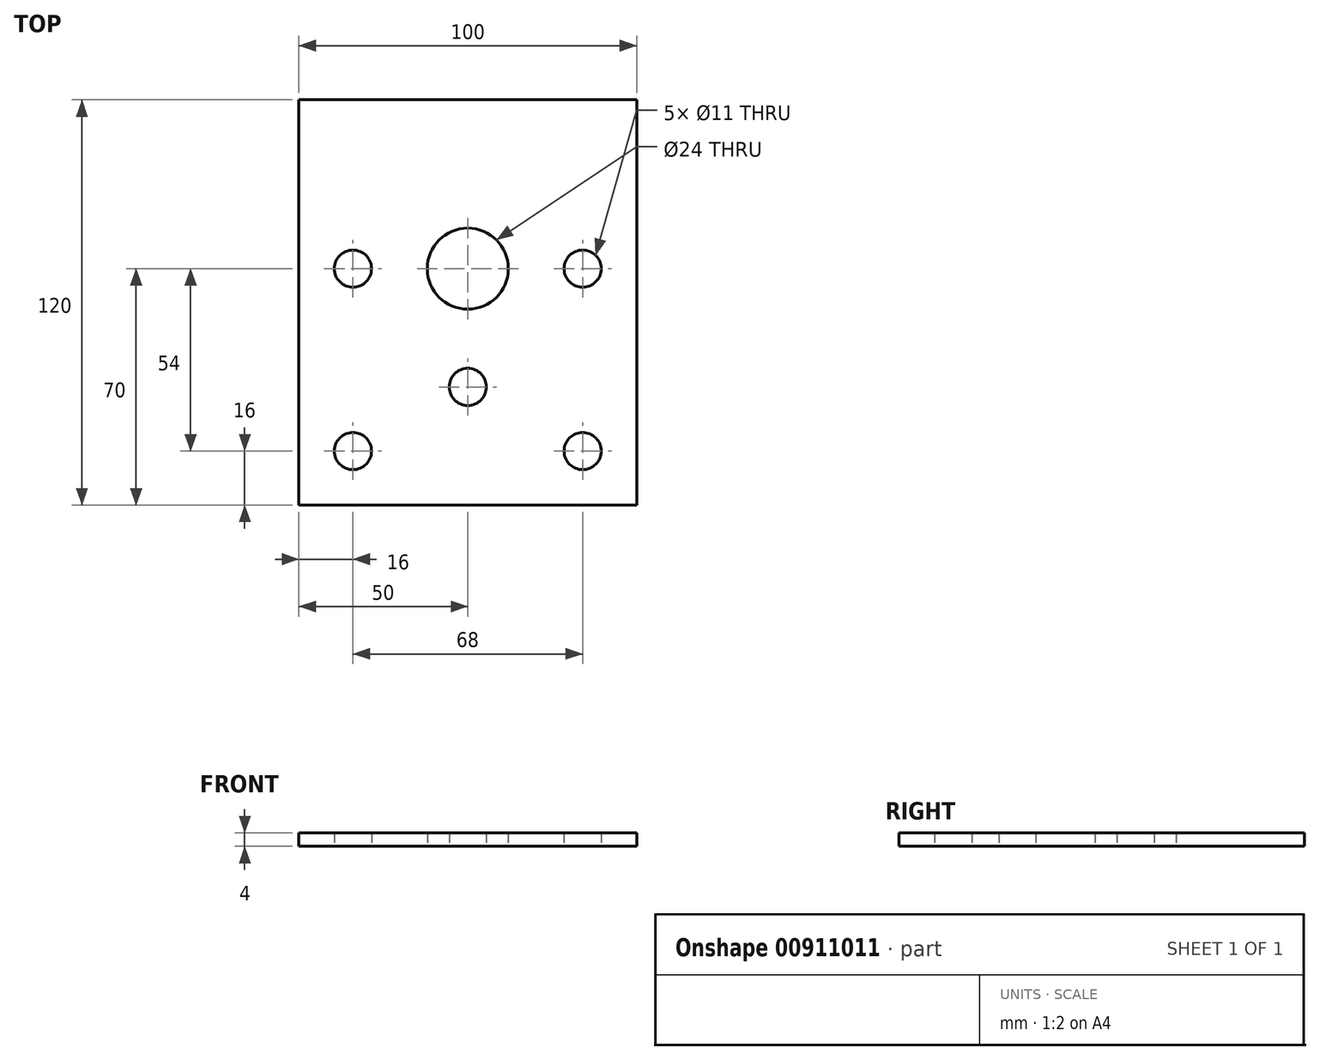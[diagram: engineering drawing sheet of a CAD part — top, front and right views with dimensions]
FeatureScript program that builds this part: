
annotation { "Feature Type Name" : "Feature", "Feature Type Description" : "" }
export const myFeature = defineFeature(function(context is Context, id is Id, definition is map)
    precondition{}
    {
        {
            var Q0;
            Q0=qCreatedBy(makeId("Top.planeOp"),FACE);
            var sketch = newSketch(context, id + "F0", { "sketchPlane" : qUnion([Q0])});
            skCircle(sketch, "E0", {"center": v(0, 0) * mm, "radius": 12 * mm});
            skLineSegment(sketch, "E1", {"start": v(0, 45.45) * mm, "end": v(0, -72.98) * mm, "construction": true});
            skLineSegment(sketch, "E2", {"start": v(0, 50) * mm, "end": v(50, 50) * mm});
            skLineSegment(sketch, "E3", {"start": v(50, 50) * mm, "end": v(50, -70) * mm});
            skLineSegment(sketch, "E4", {"start": v(50, -70) * mm, "end": v(0, -70) * mm});
            skLineSegment(sketch, "E5.MirrorCS", {"start": v(0, 50) * mm, "end": v(-50, 50) * mm});
            skLineSegment(sketch, "E6.MirrorCS", {"start": v(-50, 50) * mm, "end": v(-50, -70) * mm});
            skLineSegment(sketch, "E7.MirrorCS", {"start": v(-50, -70) * mm, "end": v(0, -70) * mm});
            skCircle(sketch, "E8", {"center": v(0, -35) * mm, "radius": 5.5 * mm});
            skCircle(sketch, "E9", {"center": v(34, 0) * mm, "radius": 5.5 * mm});
            skCircle(sketch, "E10", {"center": v(34, -54) * mm, "radius": 5.5 * mm});
            skCircle(sketch, "E11.MirrorC", {"center": v(-34, 0) * mm, "radius": 5.5 * mm});
            skCircle(sketch, "E12.MirrorC", {"center": v(-34, -54) * mm, "radius": 5.5 * mm});
            skSolve(sketch);
        }
        {
            var Q0;
            Q0=makeQuery(id+"F0.imprint","IMPRINT",FACE,{"disambiguationData":[TD([[makeQuery(id+"F0.imprint","IMPRINT",EDGE,{"derivedFrom":sQuery(id+"F0.wireOp",EDGE,"E0")}),-1.0]])]});
            extrude(context, id + "F1", {"entities" : qUnion([Q0]), "depth" : 4 * mm, "offsetDistance" : 25 * mm});
        }
    });
